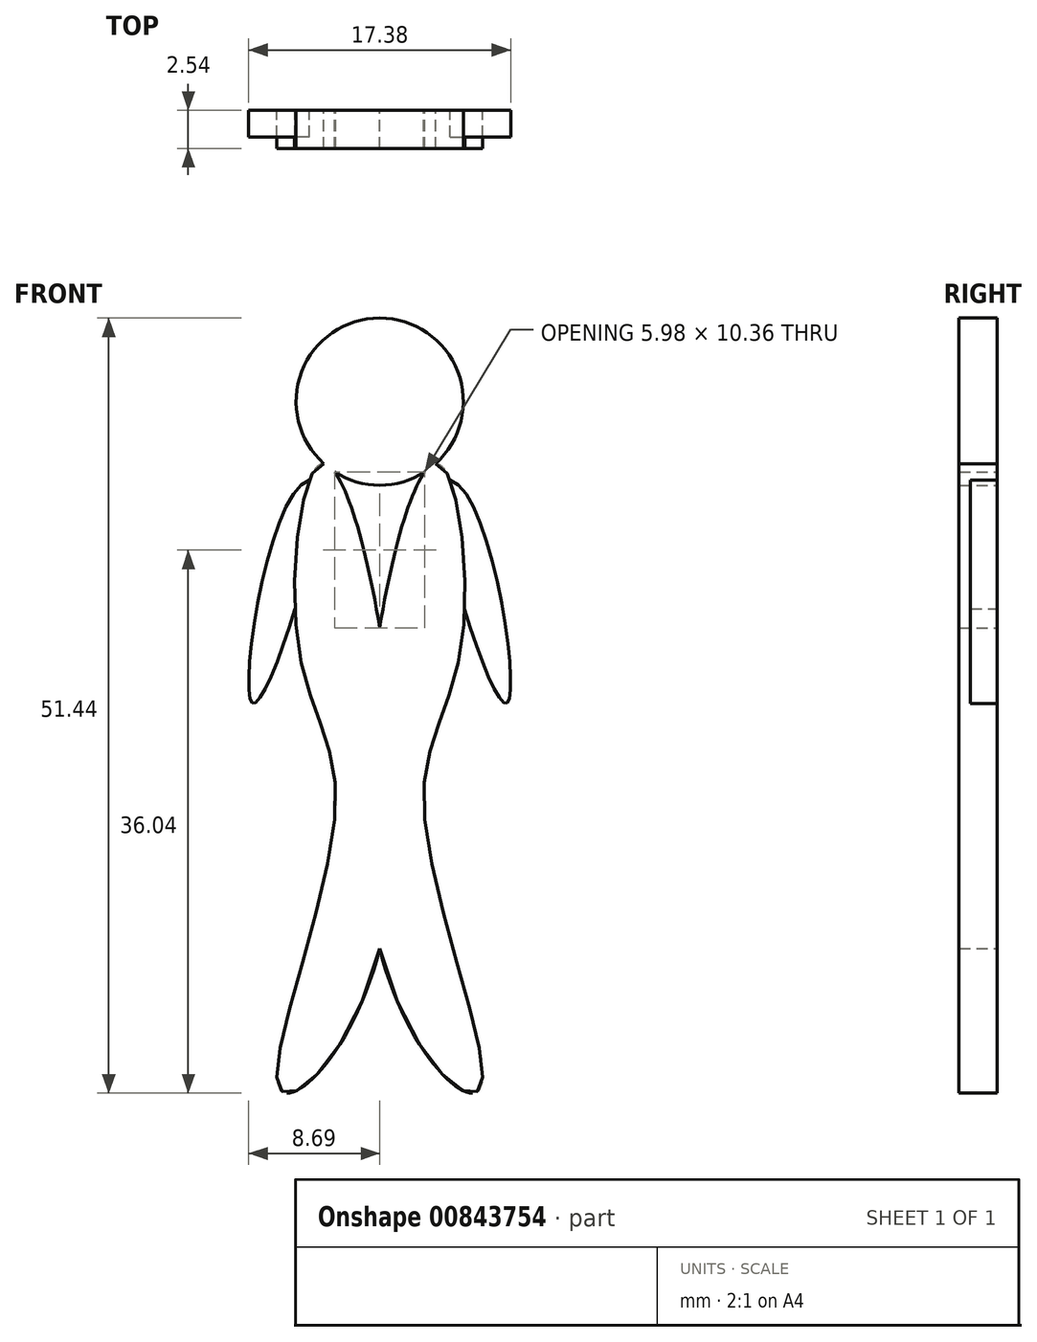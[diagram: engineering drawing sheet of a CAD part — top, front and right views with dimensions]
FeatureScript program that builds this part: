
annotation { "Feature Type Name" : "Feature", "Feature Type Description" : "" }
export const myFeature = defineFeature(function(context is Context, id is Id, definition is map)
    precondition{}
    {
        {
            var Q0;
            Q0=qCreatedBy(makeId("Front.planeOp"),FACE);
            var sketch = newSketch(context, id + "F0", { "sketchPlane" : qUnion([Q0])});
            skCircle(sketch, "E0", {"center": v(0, 52.87) * mm, "radius": 5.55 * mm});
            skFitSpline(sketch, "E1", {"points": [v(-3.7, 48.75) * mm, v(-5.43, 36.75) * mm, v(-2.95, 25.58) * mm, v(-6.67, 7.29) * mm, v(0, 16.6) * mm, v(-3.7, 48.75) * mm]});
            skFitSpline(sketch, "E2.MirrorC", {"points": [v(3.7, 48.75) * mm, v(5.43, 36.75) * mm, v(2.95, 25.58) * mm, v(6.67, 7.29) * mm, v(0, 16.6) * mm, v(3.7, 48.75) * mm]});
            skSolve(sketch);
        }
        {
            var Q0;
            Q0 = qSketchRegion(id + "F0", true);
            extrude(context, id + "F1", {"entities" : qUnion([Q0]), "depth" : 2.54 * mm, "offsetDistance" : 25.4 * mm});
        }
        {
            var Q0;
            Q0=qCreatedBy(makeId("Front.planeOp"),FACE);
            var sketch = newSketch(context, id + "F2", { "sketchPlane" : qUnion([Q0])});
            skFitSpline(sketch, "E3", {"points": [v(-2.98, 46.55) * mm, v(-4.93, 47.54) * mm, v(-8.43, 32.87) * mm, v(-4.6, 44.5) * mm, v(-4.73, 45.82) * mm, v(-2.98, 46.55) * mm]});
            skFitSpline(sketch, "E4.MirrorC", {"points": [v(2.98, 46.55) * mm, v(4.93, 47.54) * mm, v(8.43, 32.87) * mm, v(4.6, 44.5) * mm, v(4.73, 45.82) * mm, v(2.98, 46.55) * mm]});
            skSolve(sketch);
        }
        {
            var Q0;
            Q0 = qSketchRegion(id + "F2", true);
            extrude(context, id + "F3", {"entities" : qUnion([Q0]), "operationType" : NewBodyOperationType.ADD, "depth" : 1.78 * mm, "offsetDistance" : 25.4 * mm});
        }
        {
            var Q0;
            Q0=qCreatedBy(makeId("Front.planeOp"),FACE);
            var sketch = newSketch(context, id + "F4", { "sketchPlane" : qUnion([Q0])});
            skFitSpline(sketch, "E5", {"points": [v(0, 49.49) * mm, v(11.18, 52.22) * mm, v(6.91, 22.91) * mm, v(8.88, 37.46) * mm, v(5.71, 25.75) * mm, v(7.02, 37.46) * mm, v(3.74, 25.1) * mm, v(5.5, 37.9) * mm, v(2.32, 27.83) * mm, v(3.85, 38.33) * mm, v(1, 26.74) * mm, v(1.55, 39.54) * mm, v(0, 43.04) * mm, v(0, 49.49) * mm]});
            skFitSpline(sketch, "E6.MirrorC", {"points": [v(0, 49.49) * mm, v(-11.18, 52.22) * mm, v(-6.91, 22.91) * mm, v(-8.88, 37.46) * mm, v(-5.71, 25.75) * mm, v(-7.02, 37.46) * mm, v(-3.74, 25.1) * mm, v(-5.5, 37.9) * mm, v(-2.32, 27.83) * mm, v(-3.85, 38.33) * mm, v(-1, 26.74) * mm, v(-1.55, 39.54) * mm, v(0, 43.04) * mm, v(0, 49.49) * mm]});
            skSolve(sketch);
        }
        {
            var Q0;
            Q0 = qSketchRegion(id + "F4", true);
            extrude(context, id + "F5", {"entities" : qUnion([Q0]), "oppositeDirection" : true, "depth" : 3.17 * mm, "offsetDistance" : 25.4 * mm});
        }
        {
            var Q0;
            Q0=makeQuery(id+"F5.opExtrude","SWEPT_BODY",BODY,{"disambiguationData":[OSD([sQuery(id+"F4.wireOp",EDGE,"E5"),sQuery(id+"F4.wireOp",EDGE,"E6.MirrorC")])]});
            deleteBodies(context, id + "F6", {"entities" : qUnion([Q0])});
        }
    });
